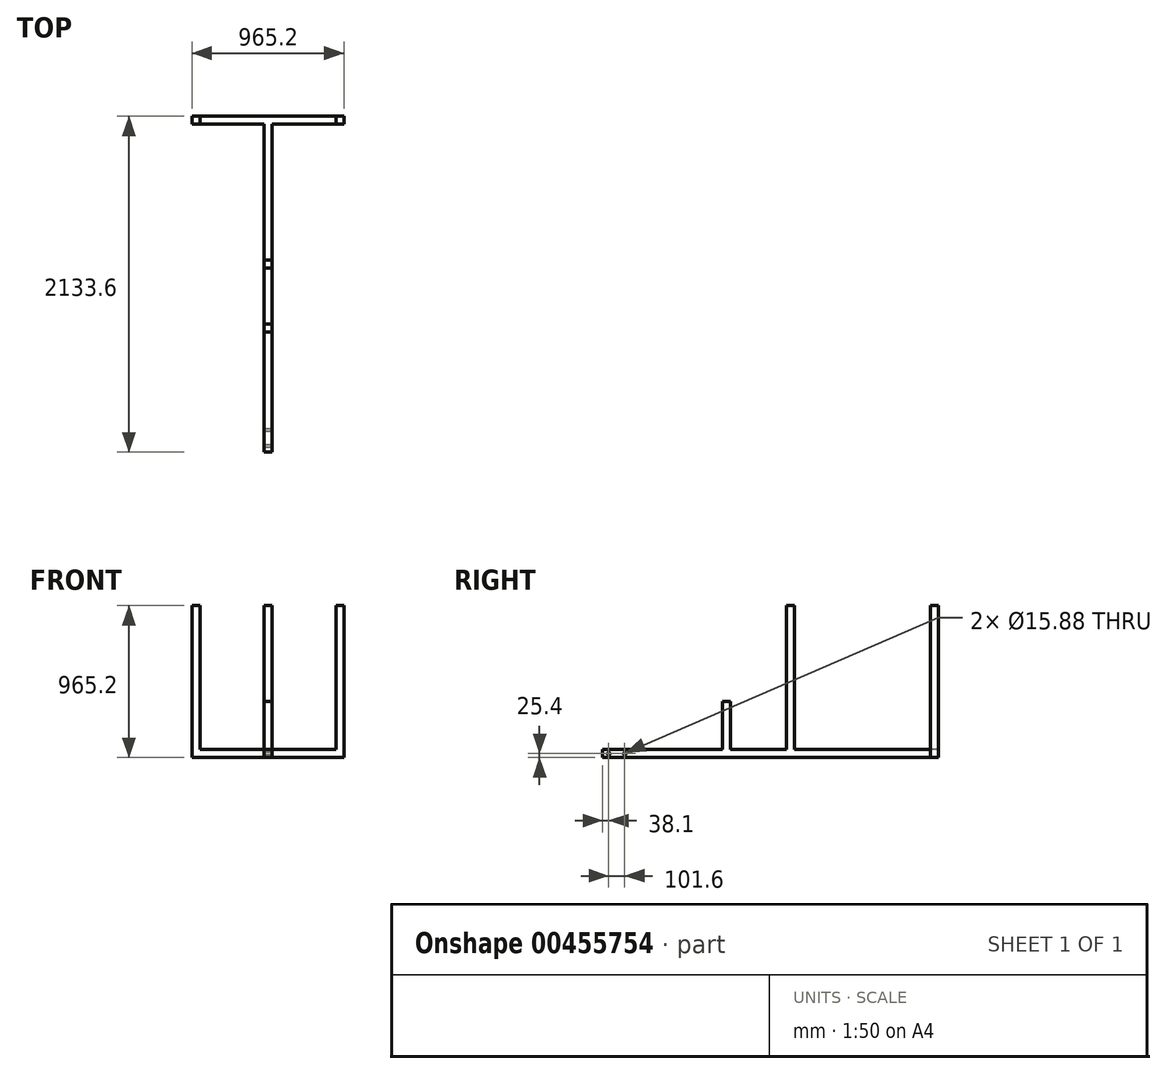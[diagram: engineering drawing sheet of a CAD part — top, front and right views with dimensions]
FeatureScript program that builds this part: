
annotation { "Feature Type Name" : "Feature", "Feature Type Description" : "" }
export const myFeature = defineFeature(function(context is Context, id is Id, definition is map)
    precondition{}
    {
        {
            var Q0;
            Q0=qCreatedBy(makeId("Top.planeOp"),FACE);
            var sketch = newSketch(context, id + "F0", { "sketchPlane" : qUnion([Q0])});
            skLineSegment(sketch, "E0.bottom", {"start": v(0, 2133.6) * mm, "end": v(-50.8, 2133.6) * mm});
            skLineSegment(sketch, "E0.top", {"start": v(0, 0) * mm, "end": v(-50.8, 0) * mm});
            skLineSegment(sketch, "E0.left", {"start": v(0, 2133.6) * mm, "end": v(0, 0) * mm});
            skLineSegment(sketch, "E0.right", {"start": v(-50.8, 2133.6) * mm, "end": v(-50.8, 0) * mm});
            skLineSegment(sketch, "E1.bottom", {"start": v(-50.8, 2133.6) * mm, "end": v(-508, 2133.6) * mm});
            skLineSegment(sketch, "E1.top", {"start": v(-50.8, 2082.8) * mm, "end": v(-508, 2082.8) * mm});
            skLineSegment(sketch, "E1.left", {"start": v(-50.8, 2133.6) * mm, "end": v(-50.8, 2082.8) * mm});
            skLineSegment(sketch, "E1.right", {"start": v(-508, 2133.6) * mm, "end": v(-508, 2082.8) * mm});
            skLineSegment(sketch, "E2.bottom", {"start": v(0, 2133.6) * mm, "end": v(457.2, 2133.6) * mm});
            skLineSegment(sketch, "E2.top", {"start": v(0, 2082.8) * mm, "end": v(457.2, 2082.8) * mm});
            skLineSegment(sketch, "E2.left", {"start": v(0, 2133.6) * mm, "end": v(0, 2082.8) * mm});
            skLineSegment(sketch, "E2.right", {"start": v(457.2, 2133.6) * mm, "end": v(457.2, 2082.8) * mm});
            skSolve(sketch);
        }
        {
            var Q0;
            Q0=makeQuery(id+"F0.imprint","IMPRINT",FACE,{"disambiguationData":[TD([[makeQuery(id+"F0.imprint","IMPRINT",EDGE,{"derivedFrom":sQuery(id+"F0.wireOp",EDGE,"E0.bottom")}),1.0]])]});
            var Q1;
            Q1=makeQuery(id+"F0.imprint","IMPRINT",FACE,{"disambiguationData":[TD([[makeQuery(id+"F0.imprint","IMPRINT",EDGE,{"derivedFrom":sQuery(id+"F0.wireOp",EDGE,"E2.bottom")}),-1.0]])]});
            var Q2;
            Q2=makeQuery(id+"F0.imprint","IMPRINT",FACE,{"disambiguationData":[TD([[makeQuery(id+"F0.imprint","IMPRINT",EDGE,{"derivedFrom":sQuery(id+"F0.wireOp",EDGE,"E1.bottom")}),1.0]])]});
            extrude(context, id + "F1", {"entities" : qUnion([Q0, Q1, Q2]), "depth" : 50.8 * mm});
        }
        {
            var Q0;
            Q0=makeQuery(id+"F1.opExtrude","CAP_FACE",FACE,{"disambiguationData":[OSD([sQuery(id+"F0.wireOp",EDGE,"E0.bottom"),sQuery(id+"F0.wireOp",EDGE,"E0.top"),sQuery(id+"F0.wireOp",EDGE,"E0.left"),sQuery(id+"F0.wireOp",EDGE,"E0.right"),sQuery(id+"F0.wireOp",EDGE,"E1.bottom"),sQuery(id+"F0.wireOp",EDGE,"E1.top"),sQuery(id+"F0.wireOp",EDGE,"E1.right"),sQuery(id+"F0.wireOp",EDGE,"E2.bottom"),sQuery(id+"F0.wireOp",EDGE,"E2.top"),sQuery(id+"F0.wireOp",EDGE,"E2.right")])],"isStart":false});
            var sketch = newSketch(context, id + "F2", { "sketchPlane" : qUnion([Q0])});
            skLineSegment(sketch, "E3.bottom", {"start": v(-508, 2133.6) * mm, "end": v(-457.2, 2133.6) * mm});
            skLineSegment(sketch, "E3.top", {"start": v(-508, 2082.8) * mm, "end": v(-457.2, 2082.8) * mm});
            skLineSegment(sketch, "E3.left", {"start": v(-508, 2133.6) * mm, "end": v(-508, 2082.8) * mm});
            skLineSegment(sketch, "E3.right", {"start": v(-457.2, 2133.6) * mm, "end": v(-457.2, 2082.8) * mm});
            skLineSegment(sketch, "E4.bottom", {"start": v(457.2, 2133.6) * mm, "end": v(406.4, 2133.6) * mm});
            skLineSegment(sketch, "E4.top", {"start": v(457.2, 2082.8) * mm, "end": v(406.4, 2082.8) * mm});
            skLineSegment(sketch, "E4.left", {"start": v(457.2, 2133.6) * mm, "end": v(457.2, 2082.8) * mm});
            skLineSegment(sketch, "E4.right", {"start": v(406.4, 2133.6) * mm, "end": v(406.4, 2082.8) * mm});
            skSolve(sketch);
        }
        {
            var Q0;
            Q0=makeQuery(id+"F2.imprint","IMPRINT",FACE,{"disambiguationData":[TD([[makeQuery(id+"F2.imprint","IMPRINT",EDGE,{"derivedFrom":sQuery(id+"F2.wireOp",EDGE,"E3.bottom")}),1.0]])]});
            var Q1;
            Q1=makeQuery(id+"F2.imprint","IMPRINT",FACE,{"disambiguationData":[TD([[makeQuery(id+"F2.imprint","IMPRINT",EDGE,{"derivedFrom":sQuery(id+"F2.wireOp",EDGE,"E4.bottom")}),1.0]])]});
            extrude(context, id + "F3", {"entities" : qUnion([Q0, Q1]), "operationType" : NewBodyOperationType.ADD, "depth" : 914.4 * mm});
        }
        {
            var Q0;
            Q0=makeQuery(id+"F1.opExtrude","CAP_FACE",FACE,{"disambiguationData":[OSD([sQuery(id+"F0.wireOp",EDGE,"E0.bottom"),sQuery(id+"F0.wireOp",EDGE,"E0.top"),sQuery(id+"F0.wireOp",EDGE,"E0.left"),sQuery(id+"F0.wireOp",EDGE,"E0.right"),sQuery(id+"F0.wireOp",EDGE,"E1.bottom"),sQuery(id+"F0.wireOp",EDGE,"E1.top"),sQuery(id+"F0.wireOp",EDGE,"E1.right"),sQuery(id+"F0.wireOp",EDGE,"E2.bottom"),sQuery(id+"F0.wireOp",EDGE,"E2.top"),sQuery(id+"F0.wireOp",EDGE,"E2.right")])],"isStart":false});
            var sketch = newSketch(context, id + "F4", { "sketchPlane" : qUnion([Q0])});
            skLineSegment(sketch, "E5.bottom", {"start": v(-50.8, 1219.2) * mm, "end": v(0, 1219.2) * mm});
            skLineSegment(sketch, "E5.top", {"start": v(-50.8, 1168.4) * mm, "end": v(0, 1168.4) * mm});
            skLineSegment(sketch, "E5.left", {"start": v(-50.8, 1219.2) * mm, "end": v(-50.8, 1168.4) * mm});
            skLineSegment(sketch, "E5.right", {"start": v(0, 1219.2) * mm, "end": v(0, 1168.4) * mm});
            skSolve(sketch);
        }
        {
            var Q0;
            Q0 = qSketchRegion(id + "F4", true);
            extrude(context, id + "F5", {"entities" : qUnion([Q0]), "operationType" : NewBodyOperationType.ADD, "depth" : 914.4 * mm});
        }
        {
            var Q0;
            {var subQ0=sQuery(id+"F0.wireOp",EDGE,"E0.right");var subQ1=sQuery(id+"F0.wireOp",EDGE,"E0.left");var subQ2=sQuery(id+"F0.wireOp",EDGE,"E0.top");Q0=makeQuery(id+"F5.boolean.opBoolean","SPLIT",FACE,{"disambiguationData":[TD([makeQuery(id+"F1.opExtrude","SWEPT_FACE",FACE,{"disambiguationData":[OSD([subQ2])]})])],"derivedFrom":makeQuery(id+"F1.opExtrude","CAP_FACE",FACE,{"disambiguationData":[OSD([sQuery(id+"F0.wireOp",EDGE,"E0.bottom"),subQ2,subQ1,subQ0,sQuery(id+"F0.wireOp",EDGE,"E1.bottom"),sQuery(id+"F0.wireOp",EDGE,"E1.top"),sQuery(id+"F0.wireOp",EDGE,"E1.right"),sQuery(id+"F0.wireOp",EDGE,"E2.bottom"),sQuery(id+"F0.wireOp",EDGE,"E2.top"),sQuery(id+"F0.wireOp",EDGE,"E2.right")])],"isStart":false})});}
            var sketch = newSketch(context, id + "F6", { "sketchPlane" : qUnion([Q0])});
            skLineSegment(sketch, "E6.bottom", {"start": v(-50.8, 812.8) * mm, "end": v(0, 812.8) * mm});
            skLineSegment(sketch, "E6.top", {"start": v(-50.8, 762) * mm, "end": v(0, 762) * mm});
            skLineSegment(sketch, "E6.left", {"start": v(-50.8, 812.8) * mm, "end": v(-50.8, 762) * mm});
            skLineSegment(sketch, "E6.right", {"start": v(0, 812.8) * mm, "end": v(0, 762) * mm});
            skSolve(sketch);
        }
        {
            var Q0;
            Q0=makeQuery(id+"F6.imprint","IMPRINT",FACE,{"disambiguationData":[TD([[makeQuery(id+"F6.imprint","IMPRINT",EDGE,{"derivedFrom":sQuery(id+"F6.wireOp",EDGE,"E6.bottom")}),-1.0]])]});
            extrude(context, id + "F7", {"entities" : qUnion([Q0]), "operationType" : NewBodyOperationType.ADD, "depth" : 304.8 * mm});
        }
        {
            var Q0;
            Q0=makeQuery(id+"F7.boolean.opBoolean","MERGE",FACE,{"derivedFrom":[makeQuery(id+"F5.boolean.opBoolean","MERGE",FACE,{"derivedFrom":[makeQuery(id+"F1.opExtrude","SWEPT_FACE",FACE,{"disambiguationData":[OSD([sQuery(id+"F0.wireOp",EDGE,"E0.right")])]}),makeQuery(id+"F5.opExtrude","SWEPT_FACE",FACE,{"disambiguationData":[OSD([sQuery(id+"F4.wireOp",EDGE,"E5.left")])]})]}),makeQuery(id+"F7.opExtrude","SWEPT_FACE",FACE,{"disambiguationData":[OSD([sQuery(id+"F6.wireOp",EDGE,"E6.left")])]})]});
            var sketch = newSketch(context, id + "F8", { "sketchPlane" : qUnion([Q0])});
            skCircle(sketch, "E7", {"center": v(-139.7, 25.4) * mm, "radius": 7.94 * mm});
            skPoint(sketch, "E7.centerSnap0", {"position": v(0, 25.4) * mm});
            skCircle(sketch, "E8", {"center": v(-38.1, 25.4) * mm, "radius": 7.94 * mm});
            skSolve(sketch);
        }
        {
            var Q0;
            Q0=makeQuery(id+"F8.imprint","IMPRINT",FACE,{"disambiguationData":[TD([[makeQuery(id+"F8.imprint","IMPRINT",EDGE,{"derivedFrom":sQuery(id+"F8.wireOp",EDGE,"E7")}),1.0]])]});
            var Q1;
            Q1=makeQuery(id+"F8.imprint","IMPRINT",FACE,{"disambiguationData":[TD([[makeQuery(id+"F8.imprint","IMPRINT",EDGE,{"derivedFrom":sQuery(id+"F8.wireOp",EDGE,"E8")}),1.0]])]});
            extrude(context, id + "F9", {"entities" : qUnion([Q0, Q1]), "operationType" : NewBodyOperationType.REMOVE, "oppositeDirection" : true, "depth" : 50.8 * mm});
        }
    });
